# Revit family: Pump_Commercial-Sewage_Dewatering-Zoeller-400_Single_Seal_Series
name_source: partatom
category: Mechanical Equipment
units: mm (PartAtom-declared; Revit-internal decimal feet)

## family parameters
Always vertical = No
Cut with Voids When Loaded = No
OmniClass Number = 23.60.30.21
OmniClass Title = Pumps
Part Type = Normal
Room Calculation Point = No
Round Connector Dimension = Use Radius
Shared = Yes
Work Plane-Based = Yes

## types (6) — shared parameters
Assembly Code = D2090
Cooling = Oil filled
Default Elevation = 0"
Description = Single seal submersible sewage or dewatering pumps.
Discharge Diameter = 4"
Discharge Height = 6 1/4"
Discharge Radius = 2"
Discharge Size = 4 Horizontal ANSI flange
Gasket = Neoprene square ring and gasket
Height = 26"
Hertz = 60
Impeller = Cast iron
Impeller Type = Non-clogging vortex
Installation Type = Floor Mounted
Insulation = Class B
Length = 16 1/8"
Lower Bearing = Ball bearing
Manufacturer = Zoeller
Material = Cast Iron-Zoeller-Powder Coated Epoxy
Max. Operating Temp. = 130° F (54° C)
Mechanical Seals = Carbon and ceramic
Motor Protection = Auto reset thermal overload (1ph)
Motor Shaft = 1117 carbon steel
Operation = Nonautomatic
Price = Prices may vary. Please consult Manufacturer Representative for most up-to-date price list.
Product Documentation Link = https://www.zoellerpumps.com
Product Page URL = http://www.zoellerpumps.com
RPM = 1750
Revised Date = 03/01/2023
Solid Handling = 3 (76 mm) spherical solids
Type SOW Power Cord Length = 240"
URL = http://www.zoellerpumps.com
Upper Bearing = Ball bearing
Warranty Information = 18 Months (Limited)
Waste Connection = Yes
Width = 12 1/2"

## per-type parameters (varying)
| type | Amps | Apparent Load | Cord Type | Finish | Max Flow @ 5' | Max. Head | Model | Motor | Phase | Type | Voltage |
| I404 - 200V/1Ph/14.4A/2HP | 14 A | 2880 VA | 1 Ph-UL listed 3-wire neoprene cord and plug | Cast Iron-Zoeller-Powder Coated Epoxy | 300 GPM | 396" | I404 | 2 HP | 1 | Permanent Split Capacitor | 200 V |
| E405 - 230V/1Ph/19.0A/3HP | 19 A | 4370 VA | 1 Ph-UL listed 3-wire neoprene cord | Cast Iron-Zoeller-Powder Coated Epoxy | 361 GPM | 456 | E405 | 3 HP | 1 | Permanent split capacitor | 230 V |
| I405 - 200V/1Ph/20.2A/3HP | 20 A | 4040 VA | 1 Ph-UL listed 3-wire neoprene cord | <By Category> | 361 GPM | 456 | I405 | 3 HP | 1 | Permanent split capacitor | 200 V |
| J405 - 200V/3Ph/14.8A/3HP | 15 A | 2960 VA | 3 Ph-4-wire with no plug | Cast Iron-Zoeller-Powder Coated Epoxy | 361 GPM | 456 | J405 | 3 HP | 3 | 3 Ph | 200 V |
| F405 - 230V/3Ph/12.2A/3HP | 12 A | 2806 VA | 3 Ph-4-wire with no plug | Cast Iron-Zoeller-Powder Coated Epoxy | 361 GPM | 456 | F405 | 3 HP | 3 | 3 Ph | 230 V |
| G405 - 460V/3Ph/6.1A/3HP | 6 A | 2806 VA | 3 Ph-4-wire with no plug | Cast Iron-Zoeller-Powder Coated Epoxy | 361 GPM | 456 | G405 | 3 HP | 3 | 3 Ph | 460 V |

## geometry (parser evidence)
native form markers: Sweep x1
no freeform markers — native parametric forms only
